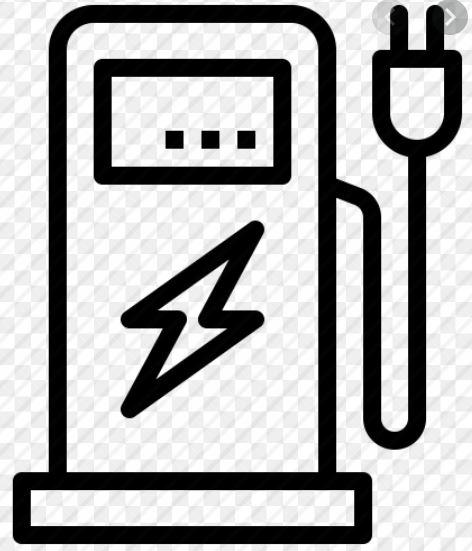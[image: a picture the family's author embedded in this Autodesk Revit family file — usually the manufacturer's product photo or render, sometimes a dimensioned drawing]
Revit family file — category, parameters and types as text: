
# Revit family: Building-RicaricaVeicoliElettrici-GEWISS-JOINON-ICON_CAVO
name_source: partatom
category: Apparecchi elettrici
units: mm (PartAtom-declared; Revit-internal decimal feet)

## family parameters
Condiviso = No
Host = Superficie
Mantenere orientamento annotazione = Sì
Punto di calcolo locali = Sì
Quota connettore circolare = Usa diametro
Taglio con vuoti quando caricato = No
Tipo di parte = Normale

## types (1)
- Building-RicaricaVeicoliElettrici-GEWISS-JOINON-ICON_CAVO
    Attivazione ricarica = Accesso Libero, con gestione dinamica dei carichi
    BLOCCO = B=C
    Caratteristiche meccaniche = -
    Codice Electrocod = 2242
    Colore = Grigio scuro
    Connettività: = BLE
    Contatore di energia = Attualmente non presente
    Corrente erogata (max): = 16 Ampere
    Corrente nominale: = 16 Ampere
    DC Leakage check = Si
    Descrizione = JOINON I-CON AUTOSTART DLM 11KW CB
    FORMULA = 1000 mm  [stored 3.28084 ft]
    Grado di protezione = IP55
    Human Interface = Led RGB
    IDF = 217c3640-93e3-4810-880b-6c3ee594507f
    INPUT: = -
    Immagine tipo = ICON_S.jpg
    L = 155 mm  [stored 0.50853 ft]
    Materiale = Termoplastico (origine Post Industrial)
    Modello = GWJ3113A
    Morsettiera: = 5 x 10 mm²
    N. Prese Tipo 2 = 1
    N.poli = 1
    Numero di prese (tipo) = 1 (connettore Tipo 2 con cavo 5 mt)
    OUTPUT : = -
    POMELLO = bianco
    PRESA = Giallo
    Personalizzabile: = SI (frontale)
    Potenza complessiva: = 11 Chilowatt
    Potenza di ricarica = 11 kW
    Potenza max = 11 Chilowatt
    Produttore = GEWISS S.p.A.
    Prospetto di default = 1219 mm
    Protezione magnetotermica = Attualmente non presente
    Protezioni = DC Leak 6mA
    Resistenza agli urti = IK10
    Riarmo protezioni da remoto = Attualmente non presente
    STRUTTURA = RAL - 7035
    STRUTTURA ALTA = blue
    Spostamento_S = 1500 mm  [stored 4.92126 ft]
    Temperatura di utilizzo = -25 +50 °C
    Tensione nominale = 400 Volt
    Tensione nominale di isolamento (Ui) = 400 Volt
    Tipo di installazione e montaggio = A parete o su supporto a pavimento
    Tipo di protezione differenziale = Attualmente non presente
    Tipologia Presa: = Tipo 2 mobile con cavo
    Trattamento esterno = No
    URL = https://www.gewiss.com
    VETRO = Vetro
    Versione file RFA = 19.4
    Voltaggio = 0 V
    W = 115 mm  [stored 0.377297 ft]

note: [stored X ft] marks values corroborated as IEEE doubles in the binary element streams (Revit-internal decimal feet)

## geometry (parser evidence)
native form markers: Sweep x3
no freeform markers — native parametric forms only
